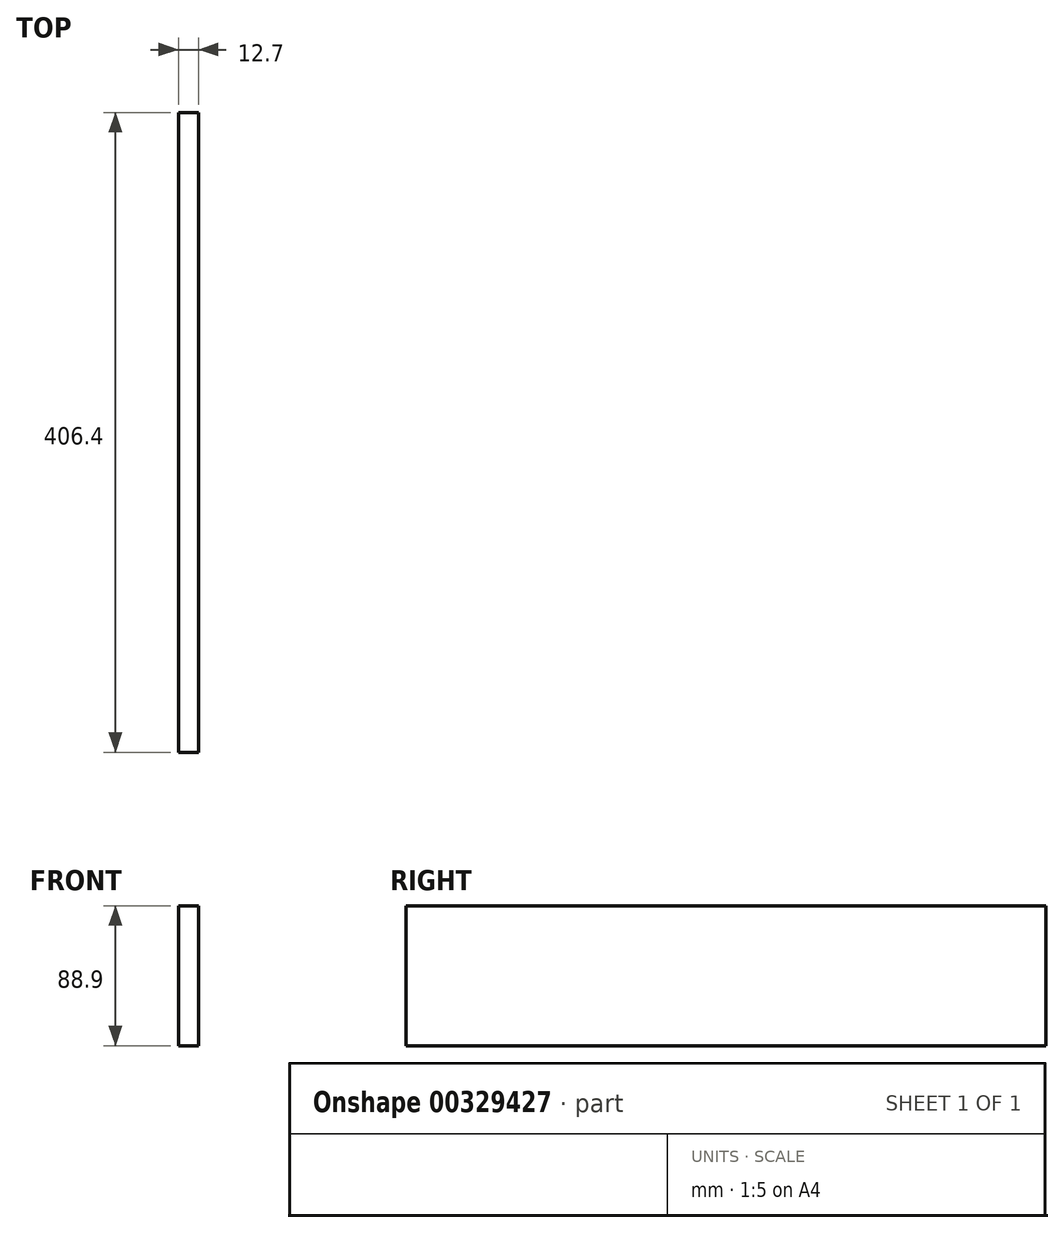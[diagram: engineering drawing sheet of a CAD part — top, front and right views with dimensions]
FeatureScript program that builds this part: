
annotation { "Feature Type Name" : "Feature", "Feature Type Description" : "" }
export const myFeature = defineFeature(function(context is Context, id is Id, definition is map)
    precondition{}
    {
        {
            var Q0;
            Q0=qCreatedBy(makeId("Right.planeOp"),FACE);
            var sketch = newSketch(context, id + "F0", { "sketchPlane" : qUnion([Q0])});
            skLineSegment(sketch, "E0.bottom", {"start": v(-203.2, 44.45) * mm, "end": v(203.2, 44.45) * mm});
            skLineSegment(sketch, "E0.top", {"start": v(-203.2, -44.45) * mm, "end": v(203.2, -44.45) * mm});
            skLineSegment(sketch, "E0.left", {"start": v(-203.2, 44.45) * mm, "end": v(-203.2, -44.45) * mm});
            skLineSegment(sketch, "E0.right", {"start": v(203.2, 44.45) * mm, "end": v(203.2, -44.45) * mm});
            skPoint(sketch, "E0.middle", {"position": v(0, 0) * mm});
            skSolve(sketch);
        }
        {
            var Q0;
            Q0=qSketchRegion(id+"F0",true);
            extrude(context, id + "F1", {"entities" : qUnion([Q0]), "depth" : 12.7 * mm});
        }
    });
